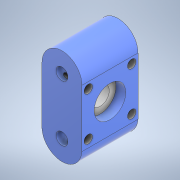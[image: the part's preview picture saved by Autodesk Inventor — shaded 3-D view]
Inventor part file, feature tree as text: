
AUTODESK INVENTOR PART (.ipt)
format: ipt  version: 2021 (Build 250183000, 183)  size: 317,952 bytes
history: native  units: mm
features: extrude x18, sketch x15, projected_geometry x11
ambient origin geometry x8: Origin, YZ Plane, XZ Plane, XY Plane, X Axis, Y Axis, Z Axis, Center Point
bodies: Solid1 (feature_tree)
feature tree (44):
  sketch  "Sketch1"  dims[d0=8.5mm d1=20.0mm]
  extrude  "Extrusion1"  Depth=20.0mm
  sketch  "Sketch2"  dims[d2=20.0mm d3=40.0mm]
  extrude  "Extrusion3"  Depth=40.0mm
  extrude  "Extrusion5"  Depth=15.0mm
  extrude  "Extrusion6"  Depth=22.5mm
  extrude  "Extrusion7"  Depth=3.0mm
  extrude  "Extrusion8"  Depth=11.25mm
  extrude  "Extrusion9"  Depth=15.0mm
  extrude  "Extrusion10"  Depth=8.5mm
  extrude  "Extrusion11"  Depth=3.0mm
  extrude  "Extrusion12"  Depth=3.0mm TaperAngle=0.0deg
  extrude  "Extrusion13"  Depth=3.0mm TaperAngle=0.0deg
  extrude  "Extrusion14"  Depth=10.0mm TaperAngle=0.0deg
  extrude  "Extrusion15"  Depth=4.0mm TaperAngle=0.0deg
  extrude  "Extrusion16"  Depth=10.0mm TaperAngle=0.0deg
  extrude  "Extrusion17"  Depth=4.0mm TaperAngle=0.0deg
  extrude  "Extrusion18"  Depth=4.0mm
  extrude  "Extrusion19"  Depth=4.0mm
  extrude  "Extrusion20"  Depth=4.0mm
  sketch  "Sketch3"  dims[d4=15.0mm d5=15.0mm]
  sketch  "Sketch4"  dims[d6=40.0mm d7=22.5mm]
  sketch  "Sketch5"  dims[d8=3.0mm d9=0.0mm d10=26.0mm]
  sketch  "Sketch6"  dims[d22=6.0mm d23=0.0mm d27=11.25mm]
  projected_geometry  "Projected Loop1"
  sketch  "Sketch7"  dims[d28=15.0mm d29=15.0mm]
  projected_geometry  "Projected Loop2"
  projected_geometry  "Projected Loop3"
  sketch  "Sketch8"  dims[d30=8.5mm d31=8.5mm]
  projected_geometry  "Projected Loop4"
  projected_geometry  "Projected Loop5"
  sketch  "Sketch9"  dims[d32=3.0mm d33=0.0mm d34=8.5mm]
  projected_geometry  "Projected Loop6"
  projected_geometry  "Projected Loop7"
  sketch  "Sketch10"  dims[d35=3.0mm d36=0.0mm d37=3.0mm d38=0.0mm]
  projected_geometry  "Projected Loop8"
  projected_geometry  "Projected Loop9"
  sketch  "Sketch11"  dims[d39=3.0mm d40=0.0mm d41=3.0mm d42=0.0mm]
  projected_geometry  "Projected Loop10"
  sketch  "Sketch12"  dims[d43=3.0mm d44=0.0mm d45=10.0mm d46=0.0mm]
  projected_geometry  "Projected Loop11"
  sketch  "Sketch13"  dims[d47=4.0mm d48=0.0mm d49=4.0mm d50=0.0mm]
  sketch  "Sketch14"  dims[d51=10.0mm d52=0.0mm d53=10.0mm d54=0.0mm]
  sketch  "Sketch15"  dims[d55=4.0mm d56=0.0mm d57=4.0mm d58=0.0mm d59=15.5mm d60=15.5mm d61=31.0mm d62=31.0mm d63=31.0mm d64=2.9mm d65=2.9mm d66=2.9mm d67=2.9mm d68=0.0mm d69=0.0mm d70=13.0mm d71=10.0mm d72=0.0mm d73=6.0mm d74=6.0mm d75=6.0mm d76=6.0mm d77=4.0mm d78=0.0mm]
